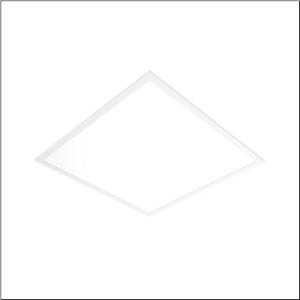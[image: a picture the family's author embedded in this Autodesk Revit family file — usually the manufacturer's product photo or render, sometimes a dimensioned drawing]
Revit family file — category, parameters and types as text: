
# Revit family: apollon_r__41_51mh11w72343_11b4
name_source: partatom
category: Lighting Fixtures
units: mm (PartAtom-declared; Revit-internal decimal feet)

## family parameters
Cut with Voids When Loaded = No
Host = Face
Light Source = No
Part Type = Normal
Room Calculation Point = No
Round Connector Dimension = Use Diameter
Shared = No

## types (1)
- Apollon® 41 (1 x LED, 3500 lm, 28.5 W, 3000K)
    Apparent Load = 29 VA
    CIE Flux Codes = 61 87 97 100 100
    Color Rendering = 80
    Color Temperature = 3000K
    Default Elevation = 1800 mm
    Description = Apollon® 41, office luminaire, primary optical cover: prismatic diffuser, of PS, light emission: direct distribution, primary light characteristic: symmetric, installation type: lay-in mounting, LED, rated luminous flux: 3.500lm, luminous efficacy: 123lm/W, light colour: 830, colour temperature: 3000K, with terminal, 3-pole, mains connection: 220..240V, AC, 50/60Hz, housing, of aluminium section, traffic white (RAL 9016), module: M625, length: 620mm, width: 620mm, height: 40mm, housing upper side, of sheet steel, protection rating (complete): IP20, protection rating (lamp compartment, on room side): IP40, insulation class (complete): insulation class II (safety insulation), certification: CE, ENEC, permissible operating ambient temperature: -20..+40°C, packaging unit: 1 piece
    Height = 0 mm  [stored 0 ft]
    Lamp = 1 x LED
    Lamp Light Flux = 3500 lm
    Lamp Power = 28.5 W
    Lamp count = 1
    Length = 620 mm
    Luminous efficacy = 123 lm/W
    Manufacturer = Siteco
    ModVariant = No
    Model = 51MH11W72343
    Mounting Place = Ceiling
    Mounting Type = Recessed
    Number of Poles = 1
    OnlyDefault = Yes
    Power Factor = 1
    Product Name = Apollon® 41
    Product group = office luminaire | ceiling recessed
    ProductGroupID = 401
    Protection Class = Protection class II
    Protection Degree = IP 20
    RLX_Detail_Level = 1
    RLX_Emergency_Light_Flux = 0 lm
    RLX_Emergency_Type = 0
    RLX_Emergency_Type_DB = No
    RlxData = <blob elided: 12177 chars, md5=a462c8d9>
    Socket = socket
    Standby Power = 0 W
    System Light Flux = 3500 lm
    System Power = 29 W
    Type Comments = Product without accessories
    Type Image = l_1291024.jpg
    URL = http://relux.com
    VarID = ---
    Voltage = 0 V
    Weight = 0.00 kg
    Width = 620 mm

note: [stored X ft] marks values corroborated as IEEE doubles in the binary element streams (Revit-internal decimal feet)

## geometry (parser evidence)
native form markers: Sweep x11
no freeform markers — native parametric forms only
